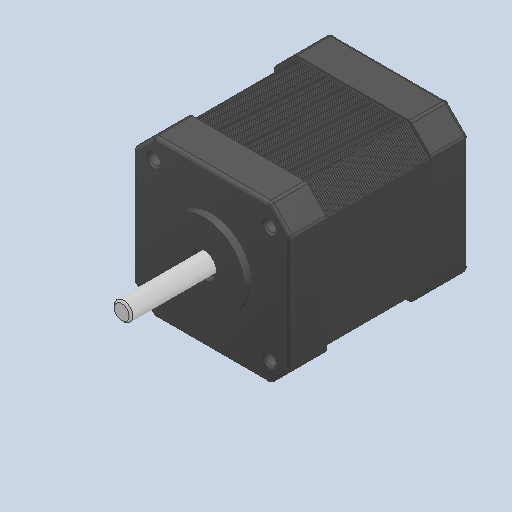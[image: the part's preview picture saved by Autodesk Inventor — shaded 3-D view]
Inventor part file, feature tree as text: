
AUTODESK INVENTOR PART (.ipt)
format: ipt  version: 2022 (Build 260153000, 153)  size: 728,576 bytes
history: imported  units: in
note: dims shown in document units (in); Inventor stores cm internally (conversion verified against a paired STEP export)
features: sketch x4, imported_body x1
ambient origin geometry x8: Origin, YZ Plane, XZ Plane, XY Plane, X Axis, Y Axis, Z Axis, Center Point
bodies: Solid1 (imported_parasolid), Body1 (imported_parasolid)
feature tree (5):
  sketch  "Sketch1"
  sketch  "Sketch2"
  sketch  "Sketch3"
  sketch  "Sketch4"
  imported_body  NMx_Import_Brep_tag  [imported B-rep: ~13 faces, bbox_mm=[3.7, 9.8, 0.0]]
